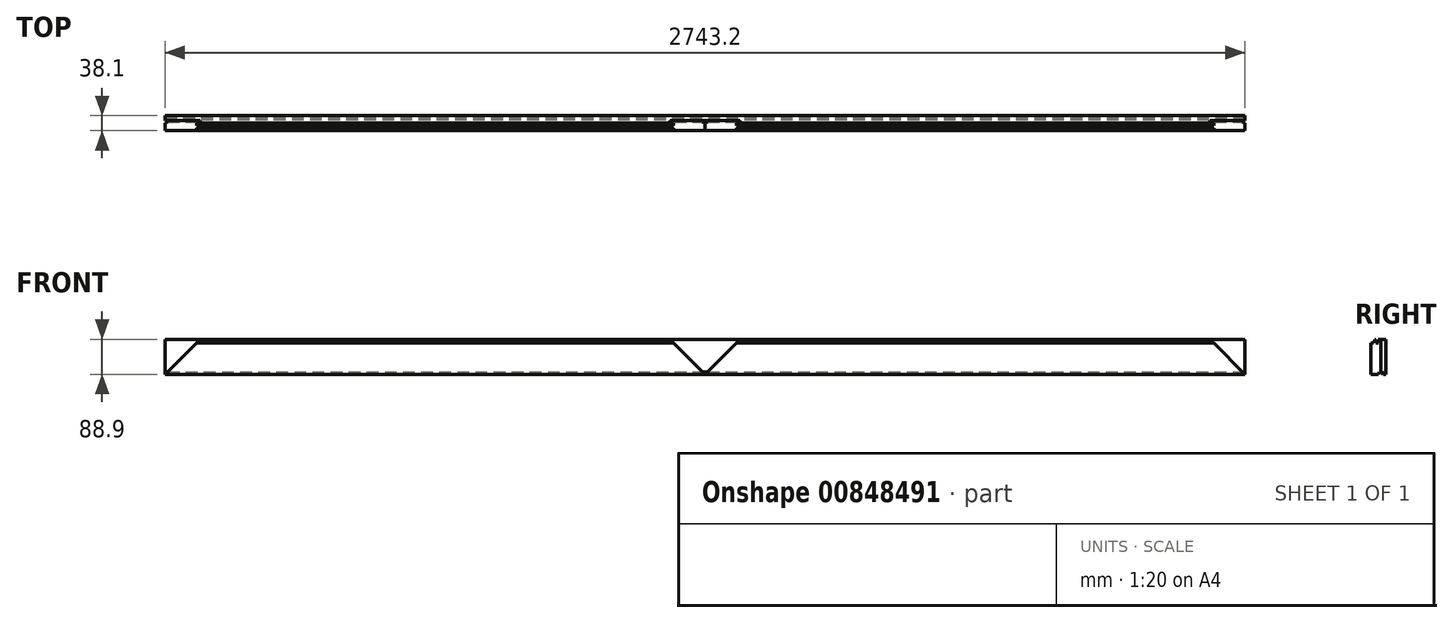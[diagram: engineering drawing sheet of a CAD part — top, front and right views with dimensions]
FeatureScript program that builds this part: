
annotation { "Feature Type Name" : "Feature", "Feature Type Description" : "" }
export const myFeature = defineFeature(function(context is Context, id is Id, definition is map)
    precondition{}
    {
        {
            var Q0;
            Q0=qCreatedBy(makeId("Front.planeOp"),FACE);
            var sketch = newSketch(context, id + "F0", { "sketchPlane" : qUnion([Q0])});
            skLineSegment(sketch, "E0.bottom", {"start": v(-1371.6, 44.45) * mm, "end": v(1371.6, 44.45) * mm});
            skLineSegment(sketch, "E0.top", {"start": v(-1371.6, -44.45) * mm, "end": v(1371.6, -44.45) * mm});
            skLineSegment(sketch, "E0.left", {"start": v(-1371.6, 44.45) * mm, "end": v(-1371.6, -44.45) * mm});
            skLineSegment(sketch, "E0.right", {"start": v(1371.6, 44.45) * mm, "end": v(1371.6, -44.45) * mm});
            skPoint(sketch, "E0.middle", {"position": v(0, 0) * mm});
            skSolve(sketch);
        }
        {
            var Q0;
            Q0 = qSketchRegion(id + "F0", true);
            extrude(context, id + "F1", {"entities" : qUnion([Q0]), "oppositeDirection" : true, "depth" : 38.1 * mm, "offsetDistance" : 25.4 * mm});
        }
        {
            var Q0;
            Q0=makeQuery(id+"F1.opExtrude","SWEPT_FACE",FACE,{"disambiguationData":[OSD([sQuery(id+"F0.wireOp",EDGE,"E0.right")])]});
            var sketch = newSketch(context, id + "F2", { "sketchPlane" : qUnion([Q0])});
            skLineSegment(sketch, "E1", {"start": v(22.22, -38.1) * mm, "end": v(19.05, -44.45) * mm});
            skLineSegment(sketch, "E2", {"start": v(31.75, -44.45) * mm, "end": v(28.57, -38.1) * mm});
            skLineSegment(sketch, "E3", {"start": v(22.22, -38.1) * mm, "end": v(28.57, -38.1) * mm});
            skLineSegment(sketch, "E4", {"start": v(31.75, -44.45) * mm, "end": v(19.05, -44.45) * mm});
            skSolve(sketch);
        }
        {
            var Q0;
            Q0 = qSketchRegion(id + "F2", true);
            extrude(context, id + "F3", {"entities" : qUnion([Q0]), "operationType" : NewBodyOperationType.REMOVE, "endBound" : BoundingType.THROUGH_ALL, "oppositeDirection" : true, "depth" : 25.4 * mm, "offsetDistance" : 25.4 * mm});
        }
        {
            var Q0;
            Q0=makeQuery(id+"F1.opExtrude","SWEPT_FACE",FACE,{"disambiguationData":[OSD([sQuery(id+"F0.wireOp",EDGE,"E0.right")])]});
            var sketch = newSketch(context, id + "F4", { "sketchPlane" : qUnion([Q0])});
            skLineSegment(sketch, "E5", {"start": v(0, 34.93) * mm, "end": v(6.35, 34.93) * mm});
            skLineSegment(sketch, "E6", {"start": v(12.7, 34.93) * mm, "end": v(19.05, 34.93) * mm});
            skArc(sketch, "E7", {"start": v(8.5, 39.69) * mm, "mid": v(6.91, 37.54) * mm, "end": v(6.35, 34.93) * mm});
            skLineSegment(sketch, "E8", {"start": v(12.7, 44.45) * mm, "end": v(12.7, 34.93) * mm});
            skLineSegment(sketch, "E9", {"start": v(19.05, 34.93) * mm, "end": v(19.05, 44.45) * mm});
            skLineSegment(sketch, "E10", {"start": v(10.65, 44.45) * mm, "end": v(0, 44.45) * mm});
            skLineSegment(sketch, "E11", {"start": v(0, 44.45) * mm, "end": v(0, 34.93) * mm});
            skLineSegment(sketch, "E12", {"start": v(12.7, 44.45) * mm, "end": v(19.05, 44.45) * mm});
            skArc(sketch, "E13", {"start": v(8.5, 39.69) * mm, "mid": v(10.09, 41.84) * mm, "end": v(10.65, 44.45) * mm});
            skSolve(sketch);
        }
        {
            var Q0;
            Q0 = qSketchRegion(id + "F4", true);
            extrude(context, id + "F5", {"entities" : qUnion([Q0]), "operationType" : NewBodyOperationType.REMOVE, "endBound" : BoundingType.THROUGH_ALL, "oppositeDirection" : true, "depth" : 25.4 * mm, "offsetDistance" : 25.4 * mm});
        }
        {
            var Q0;
            Q0=makeQuery(id+"F1.opExtrude","CAP_FACE",FACE,{"disambiguationData":[OSD([sQuery(id+"F0.wireOp",EDGE,"E0.bottom"),sQuery(id+"F0.wireOp",EDGE,"E0.top"),sQuery(id+"F0.wireOp",EDGE,"E0.left"),sQuery(id+"F0.wireOp",EDGE,"E0.right")])],"isStart":true});
            var sketch = newSketch(context, id + "F6", { "sketchPlane" : qUnion([Q0])});
            skLineSegment(sketch, "E14", {"start": v(-1371.6, -44.45) * mm, "end": v(-1282.7, 44.45) * mm});
            skLineSegment(sketch, "E15", {"start": v(-1282.7, 44.45) * mm, "end": v(-1371.6, 44.45) * mm});
            skLineSegment(sketch, "E16", {"start": v(-1371.6, 44.45) * mm, "end": v(-1371.6, -44.45) * mm});
            skPoint(sketch, "E17", {"position": v(-1371.6, -4.76) * mm});
            skLineSegment(sketch, "E18", {"start": v(0, 760.27) * mm, "end": v(0, -577.9) * mm, "construction": true});
            skLineSegment(sketch, "E19", {"start": v(-89, 44.45) * mm, "end": v(0, -44.55) * mm});
            skLineSegment(sketch, "E20", {"start": v(-89, 44.45) * mm, "end": v(0, 44.45) * mm});
            skLineSegment(sketch, "E21.MirrorCS", {"start": v(89, 44.45) * mm, "end": v(0, 44.45) * mm});
            skLineSegment(sketch, "E22.MirrorCS", {"start": v(89, 44.45) * mm, "end": v(0, -44.55) * mm});
            skLineSegment(sketch, "E23.MirrorCS", {"start": v(1371.6, 44.45) * mm, "end": v(1371.6, -44.45) * mm});
            skLineSegment(sketch, "E24.MirrorCS", {"start": v(1371.6, -44.45) * mm, "end": v(1282.7, 44.45) * mm});
            skLineSegment(sketch, "E25.MirrorCS", {"start": v(1282.7, 44.45) * mm, "end": v(1371.6, 44.45) * mm});
            skSolve(sketch);
        }
        {
            var Q0;
            Q0 = qSketchRegion(id + "F6", true);
            extrude(context, id + "F7", {"entities" : qUnion([Q0]), "operationType" : NewBodyOperationType.REMOVE, "oppositeDirection" : true, "depth" : 25.4 * mm, "offsetDistance" : 25.4 * mm});
        }
    });
